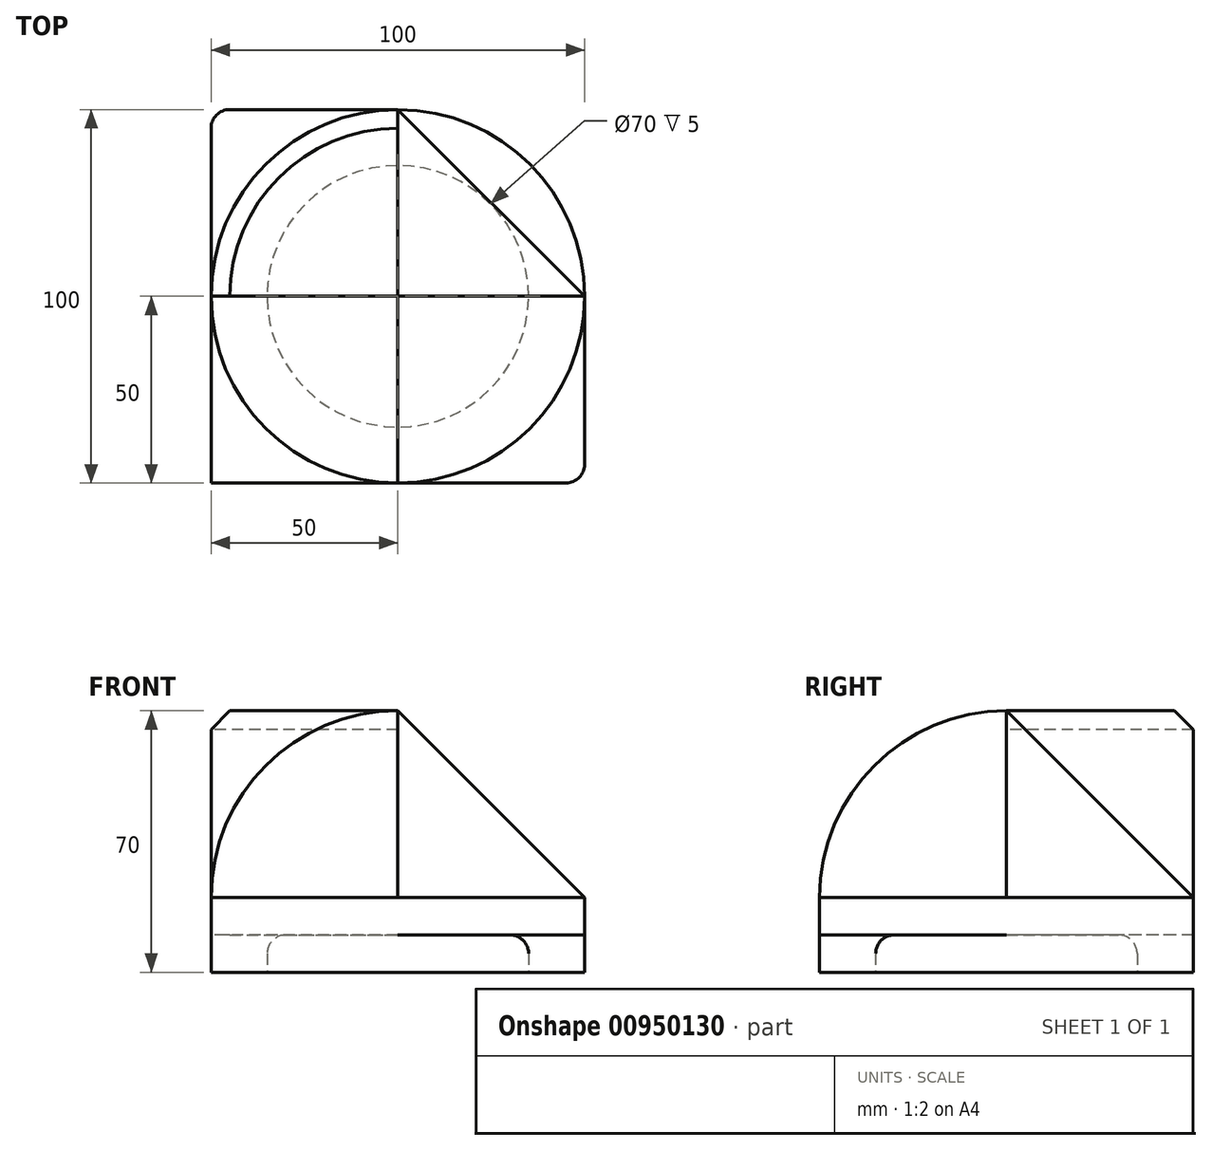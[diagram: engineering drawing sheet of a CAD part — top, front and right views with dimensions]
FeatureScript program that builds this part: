
annotation { "Feature Type Name" : "Feature", "Feature Type Description" : "" }
export const myFeature = defineFeature(function(context is Context, id is Id, definition is map)
    precondition{}
    {
        {
            var Q0;
            Q0=qCreatedBy(makeId("Top.planeOp"),FACE);
            var sketch = newSketch(context, id + "F0", { "sketchPlane" : qUnion([Q0])});
            skLineSegment(sketch, "E0.bottom", {"start": v(-50, 50) * mm, "end": v(50, 50) * mm});
            skLineSegment(sketch, "E0.top", {"start": v(-50, -50) * mm, "end": v(50, -50) * mm});
            skLineSegment(sketch, "E0.left", {"start": v(-50, 50) * mm, "end": v(-50, -50) * mm});
            skLineSegment(sketch, "E0.right", {"start": v(50, 50) * mm, "end": v(50, -50) * mm});
            skPoint(sketch, "E0.middle", {"position": v(0, 0) * mm});
            skSolve(sketch);
        }
        {
            var Q0;
            Q0 = qSketchRegion(id + "F0", true);
            extrude(context, id + "F1", {"entities" : qUnion([Q0]), "depth" : 20 * mm, "offsetDistance" : 25 * mm});
        }
        {
            var Q0;
            Q0=makeQuery(id+"F1.opExtrude","SWEPT_EDGE",EDGE,{"disambiguationData":[OSD([sQuery(id+"F0.wireOp",EDGE,"E0.bottom"),sQuery(id+"F0.wireOp",EDGE,"E0.right")])]});
            fillet(context, id + "F2", {"entities" : qUnion([Q0]), "radius" : 50 * mm, "tangentPropagation" : true, "allowEdgeOverflow" : false});
        }
        {
            var Q0;
            Q0=makeQuery(id+"F1.opExtrude","CAP_FACE",FACE,{"disambiguationData":[OSD([sQuery(id+"F0.wireOp",EDGE,"E0.bottom"),sQuery(id+"F0.wireOp",EDGE,"E0.top"),sQuery(id+"F0.wireOp",EDGE,"E0.left"),sQuery(id+"F0.wireOp",EDGE,"E0.right")])],"isStart":false});
            var sketch = newSketch(context, id + "F3", { "sketchPlane" : qUnion([Q0])});
            skArc(sketch, "E1", {"start": v(0, -50) * mm, "mid": v(35.36, -35.36) * mm, "end": v(50, 0) * mm});
            skLineSegment(sketch, "E2", {"start": v(50, 0) * mm, "end": v(50, -50) * mm});
            skLineSegment(sketch, "E3", {"start": v(50, -50) * mm, "end": v(0, -50) * mm});
            skSolve(sketch);
        }
        {
            var Q0;
            Q0 = qSketchRegion(id + "F3", true);
            extrude(context, id + "F4", {"entities" : qUnion([Q0]), "operationType" : NewBodyOperationType.REMOVE, "oppositeDirection" : true, "depth" : 10 * mm, "offsetDistance" : 25 * mm});
        }
        {
            var Q0;
            Q0=qCreatedBy(makeId("Front.planeOp"),FACE);
            var sketch = newSketch(context, id + "F5", { "sketchPlane" : qUnion([Q0])});
            skLineSegment(sketch, "E4", {"start": v(-50, 20) * mm, "end": v(0, 20) * mm});
            skLineSegment(sketch, "E5", {"start": v(0, 20) * mm, "end": v(0, 70) * mm});
            skArc(sketch, "E6", {"start": v(0, 70) * mm, "mid": v(-35.36, 55.36) * mm, "end": v(-50, 20) * mm});
            skSolve(sketch);
        }
        {
            var Q0;
            Q0 = qSketchRegion(id + "F5", true);
            var Q1;
            Q1=sQuery(id+"F5.wireOp",EDGE,"E5");
            revolve(context, id + "F6", {"operationType" : NewBodyOperationType.ADD, "surfaceOperationType" : NewSurfaceOperationType.NEW, "entities" : qUnion([Q0]), "axis" : qUnion([Q1]), "revolveType" : RevolveType.ONE_DIRECTION, "angle" : 90 * degree});
        }
        {
            var Q0;
            {var subQ0=sQuery(id+"F0.wireOp",EDGE,"E0.left");var subQ1=sQuery(id+"F0.wireOp",EDGE,"E0.right");var subQ2=sQuery(id+"F0.wireOp",EDGE,"E0.bottom");var subQ3=sQuery(id+"F0.wireOp",EDGE,"E0.top");var subQ4=makeQuery(id+"F1.opExtrude","CAP_FACE",FACE,{"disambiguationData":[OSD([subQ2,subQ3,subQ0,subQ1])],"isStart":false});var subQ5=sQuery(id+"F5.wireOp",EDGE,"E6");var subQ6=sQuery(id+"F5.wireOp",EDGE,"E5");var subQ7=sQuery(id+"F5.wireOp",EDGE,"E4");Q0=makeQuery(id+"F6.boolean.opBoolean","SPLIT",FACE,{"disambiguationData":[TD([makeQuery(id+"F1.opExtrude","SWEPT_FACE",FACE,{"disambiguationData":[OSD([subQ2])]}),subQ4,makeQuery(id+"F1.opExtrude","SWEPT_FACE",FACE,{"disambiguationData":[OSD([subQ3])]}),makeQuery(id+"F1.opExtrude","SWEPT_FACE",FACE,{"disambiguationData":[OSD([subQ0])]}),makeQuery(id+"F2.opFillet","BLEND_FACE",FACE,{"disambiguationData":[OSD([subQ2,subQ1])]}),makeQuery(id+"F6.opRevolve","CAP_FACE",FACE,{"disambiguationData":[OSD([subQ7,subQ6,subQ5])],"isStart":true}),makeQuery(id+"F6.opRevolve","CAP_FACE",FACE,{"disambiguationData":[OSD([subQ7,subQ6,subQ5])],"isStart":false}),makeQuery(id+"F6.opRevolve","SWEPT_FACE",FACE,{"disambiguationData":[OSD([subQ5])]})])],"derivedFrom":subQ4});}
            var sketch = newSketch(context, id + "F7", { "sketchPlane" : qUnion([Q0])});
            skLineSegment(sketch, "E7.bottom", {"start": v(-50, 50) * mm, "end": v(0, 50) * mm});
            skLineSegment(sketch, "E7.top", {"start": v(-50, 0) * mm, "end": v(0, 0) * mm});
            skLineSegment(sketch, "E7.left", {"start": v(-50, 50) * mm, "end": v(-50, 0) * mm});
            skLineSegment(sketch, "E7.right", {"start": v(0, 50) * mm, "end": v(0, 0) * mm});
            skSolve(sketch);
        }
        {
            var Q0;
            Q0 = qSketchRegion(id + "F7", true);
            extrude(context, id + "F8", {"entities" : qUnion([Q0]), "operationType" : NewBodyOperationType.REMOVE, "oppositeDirection" : true, "depth" : 10 * mm, "offsetDistance" : 25 * mm});
        }
        {
            var Q0;
            Q0=makeQuery(id+"F8.boolean.opBoolean","COPY",FACE,{"derivedFrom":makeQuery(id+"F8.opExtrude","CAP_FACE",FACE,{"disambiguationData":[OSD([sQuery(id+"F7.wireOp",EDGE,"E7.bottom"),sQuery(id+"F7.wireOp",EDGE,"E7.top"),sQuery(id+"F7.wireOp",EDGE,"E7.left"),sQuery(id+"F7.wireOp",EDGE,"E7.right")])],"isStart":false})});
            var sketch = newSketch(context, id + "F9", { "sketchPlane" : qUnion([Q0])});
            skLineSegment(sketch, "E8", {"start": v(-50, 0) * mm, "end": v(0, 0) * mm});
            skLineSegment(sketch, "E9", {"start": v(0, 0) * mm, "end": v(0, 50) * mm});
            skArc(sketch, "E10", {"start": v(0, 50) * mm, "mid": v(-35.36, 35.36) * mm, "end": v(-50, 0) * mm});
            skSolve(sketch);
        }
        {
            var Q0;
            Q0 = qSketchRegion(id + "F9", true);
            extrude(context, id + "F10", {"entities" : qUnion([Q0]), "operationType" : NewBodyOperationType.ADD, "depth" : 60 * mm, "offsetDistance" : 25 * mm});
        }
        {
            var Q0;
            Q0=makeQuery(id+"F10.opExtrude","CAP_EDGE",EDGE,{"disambiguationData":[OSD([sQuery(id+"F9.wireOp",EDGE,"E10")])],"isStart":false});
            chamfer(context, id + "F11", {"entities" : qUnion([Q0]), "width" : 5 * mm, "tangentPropagation" : true});
        }
        {
            var Q0;
            Q0=makeQuery(id+"F1.opExtrude","SWEPT_EDGE",EDGE,{"disambiguationData":[OSD([sQuery(id+"F0.wireOp",EDGE,"E0.bottom"),sQuery(id+"F0.wireOp",EDGE,"E0.left")])]});
            var Q1;
            Q1=makeQuery(id+"F1.opExtrude","SWEPT_EDGE",EDGE,{"disambiguationData":[OSD([sQuery(id+"F0.wireOp",EDGE,"E0.top"),sQuery(id+"F0.wireOp",EDGE,"E0.right")])]});
            fillet(context, id + "F12", {"entities" : qUnion([Q0, Q1]), "radius" : 5 * mm, "tangentPropagation" : true, "allowEdgeOverflow" : false});
        }
        {
            var Q0;
            {var subQ0=sQuery(id+"F0.wireOp",EDGE,"E0.right");var subQ1=sQuery(id+"F0.wireOp",EDGE,"E0.bottom");var subQ2=makeQuery(id+"F2.opFillet","BLEND_FACE",FACE,{"disambiguationData":[OSD([subQ1,subQ0])]});var subQ3=sQuery(id+"F0.wireOp",EDGE,"E0.top");var subQ4=makeQuery(id+"F1.opExtrude","SWEPT_FACE",FACE,{"disambiguationData":[OSD([subQ3])]});var subQ5=sQuery(id+"F0.wireOp",EDGE,"E0.left");var subQ6=makeQuery(id+"F1.opExtrude","CAP_FACE",FACE,{"disambiguationData":[OSD([subQ1,subQ3,subQ5,subQ0])],"isStart":false});var subQ7=sQuery(id+"F5.wireOp",EDGE,"E6");var subQ8=makeQuery(id+"F6.opRevolve","SWEPT_FACE",FACE,{"disambiguationData":[OSD([subQ7])]});var subQ9=makeQuery(id+"F1.opExtrude","SWEPT_FACE",FACE,{"disambiguationData":[OSD([subQ1])]});var subQ10=sQuery(id+"F5.wireOp",EDGE,"E5");var subQ11=sQuery(id+"F5.wireOp",EDGE,"E4");var subQ12=makeQuery(id+"F6.opRevolve","CAP_FACE",FACE,{"disambiguationData":[OSD([subQ11,subQ10,subQ7])],"isStart":false});Q0=makeQuery(id+"F10.boolean.opBoolean","SPLIT",FACE,{"disambiguationData":[TD([subQ4])],"derivedFrom":makeQuery(id+"F6.boolean.opBoolean","SPLIT",FACE,{"disambiguationData":[TD([subQ9,subQ6,subQ4,makeQuery(id+"F1.opExtrude","SWEPT_FACE",FACE,{"disambiguationData":[OSD([subQ5])]}),subQ2,makeQuery(id+"F6.opRevolve","CAP_FACE",FACE,{"disambiguationData":[OSD([subQ11,subQ10,subQ7])],"isStart":true}),subQ12,subQ8])],"derivedFrom":subQ6})});}
            var sketch = newSketch(context, id + "F13", { "sketchPlane" : qUnion([Q0])});
            skLineSegment(sketch, "E11", {"start": v(0, 50) * mm, "end": v(0, 0) * mm});
            skLineSegment(sketch, "E12", {"start": v(0, 0) * mm, "end": v(50, 0) * mm});
            skLineSegment(sketch, "E13", {"start": v(50, 0) * mm, "end": v(0, 50) * mm});
            skSolve(sketch);
        }
        {
            var Q0;
            Q0=makeQuery(id+"F10.opExtrude","CAP_FACE",FACE,{"disambiguationData":[OSD([sQuery(id+"F9.wireOp",EDGE,"E8"),sQuery(id+"F9.wireOp",EDGE,"E9"),sQuery(id+"F9.wireOp",EDGE,"E10")])],"isStart":false});
            var sketch = newSketch(context, id + "F14", { "sketchPlane" : qUnion([Q0])});
            skPoint(sketch, "E14", {"position": v(0, 0) * mm});
            skSolve(sketch);
        }
        {
            var Q1;
            Q1=makeQuery(id+"F13.imprint","IMPRINT",FACE,{"disambiguationData":[TD([[makeQuery(id+"F13.imprint","IMPRINT",EDGE,{"derivedFrom":sQuery(id+"F13.wireOp",EDGE,"E11")}),-1.0]])]});
            var Q2;
            Q2=sQuery(id+"F14.wireOp",VERTEX,"E14");
            loft(context, id + "F15", {"operationType" : NewBodyOperationType.ADD, "sheetProfilesArray" : [{ "sheetProfileEntities" : qUnion([Q1]) }, { "sheetProfileEntities" : qUnion([Q2]) }]});
        }
        {
            var Q0;
            Q0=makeQuery(id+"F1.opExtrude","CAP_FACE",FACE,{"disambiguationData":[OSD([sQuery(id+"F0.wireOp",EDGE,"E0.bottom"),sQuery(id+"F0.wireOp",EDGE,"E0.top"),sQuery(id+"F0.wireOp",EDGE,"E0.left"),sQuery(id+"F0.wireOp",EDGE,"E0.right")])],"isStart":true});
            var sketch = newSketch(context, id + "F16", { "sketchPlane" : qUnion([Q0])});
            skCircle(sketch, "E15", {"center": v(0, 0) * mm, "radius": 35 * mm});
            skSolve(sketch);
        }
        {
            var Q0;
            Q0 = qSketchRegion(id + "F16", true);
            extrude(context, id + "F17", {"entities" : qUnion([Q0]), "operationType" : NewBodyOperationType.REMOVE, "oppositeDirection" : true, "depth" : 10 * mm, "offsetDistance" : 25 * mm});
        }
        {
            var Q0;
            Q0=makeQuery(id+"F17.boolean.opBoolean","COPY",EDGE,{"derivedFrom":makeQuery(id+"F17.opExtrude","CAP_EDGE",EDGE,{"disambiguationData":[OSD([sQuery(id+"F16.wireOp",EDGE,"E15")])],"isStart":false})});
            fillet(context, id + "F18", {"entities" : qUnion([Q0]), "radius" : 5 * mm, "tangentPropagation" : true, "allowEdgeOverflow" : false});
        }
    });
